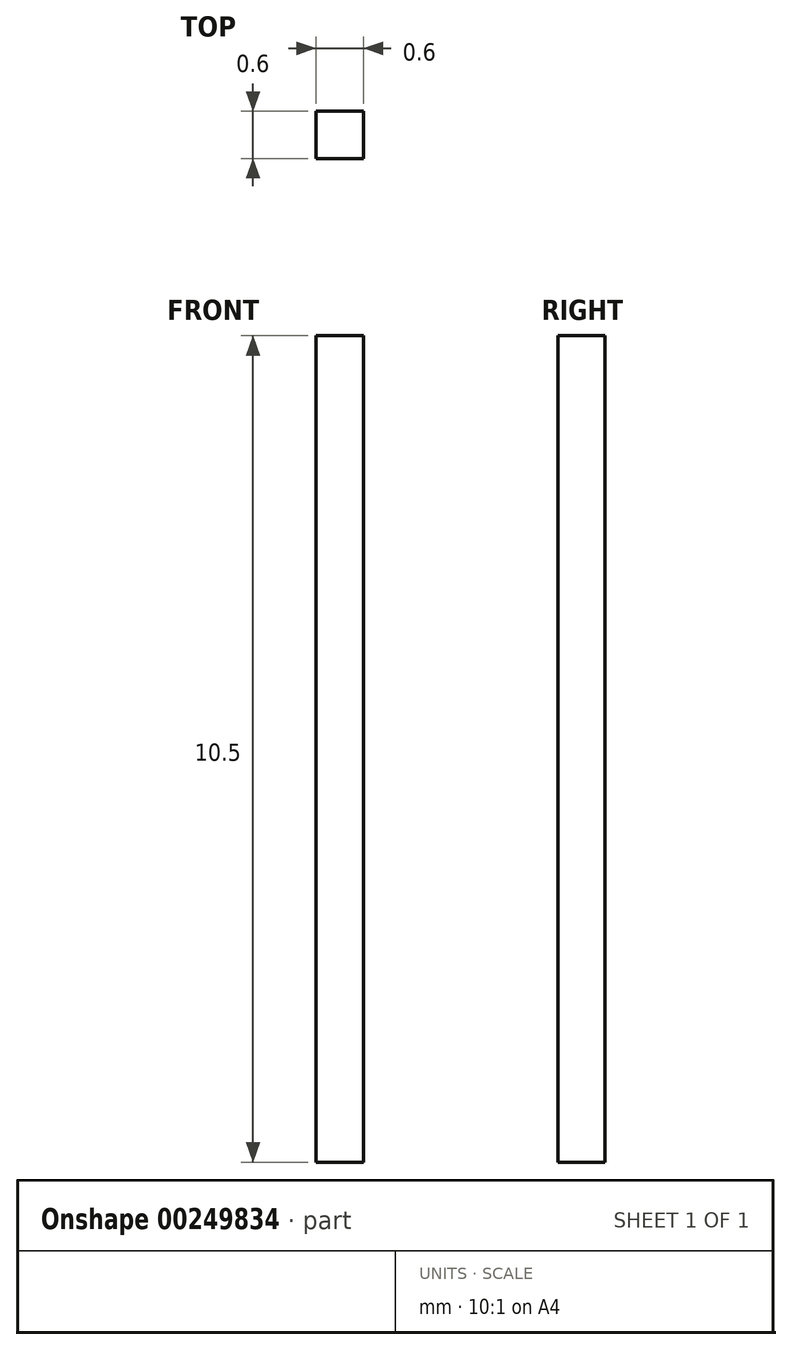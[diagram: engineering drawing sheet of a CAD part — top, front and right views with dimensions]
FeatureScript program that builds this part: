
annotation { "Feature Type Name" : "Feature", "Feature Type Description" : "" }
export const myFeature = defineFeature(function(context is Context, id is Id, definition is map)
    precondition{}
    {
        {
            var Q0;
            Q0=qCreatedBy(makeId("Top.planeOp"),FACE);
            var sketch = newSketch(context, id + "F0", { "sketchPlane" : qUnion([Q0])});
            skLineSegment(sketch, "E0.bottom", {"start": v(0, 0) * mm, "end": v(0.6, 0) * mm});
            skLineSegment(sketch, "E0.top", {"start": v(0, 0.6) * mm, "end": v(0.6, 0.6) * mm});
            skLineSegment(sketch, "E0.left", {"start": v(0, 0) * mm, "end": v(0, 0.6) * mm});
            skLineSegment(sketch, "E0.right", {"start": v(0.6, 0) * mm, "end": v(0.6, 0.6) * mm});
            skSolve(sketch);
        }
        {
            var Q0;
            Q0 = qSketchRegion(id + "F0", true);
            extrude(context, id + "F1", {"entities" : qUnion([Q0]), "depth" : 10.5 * mm});
        }
    });
